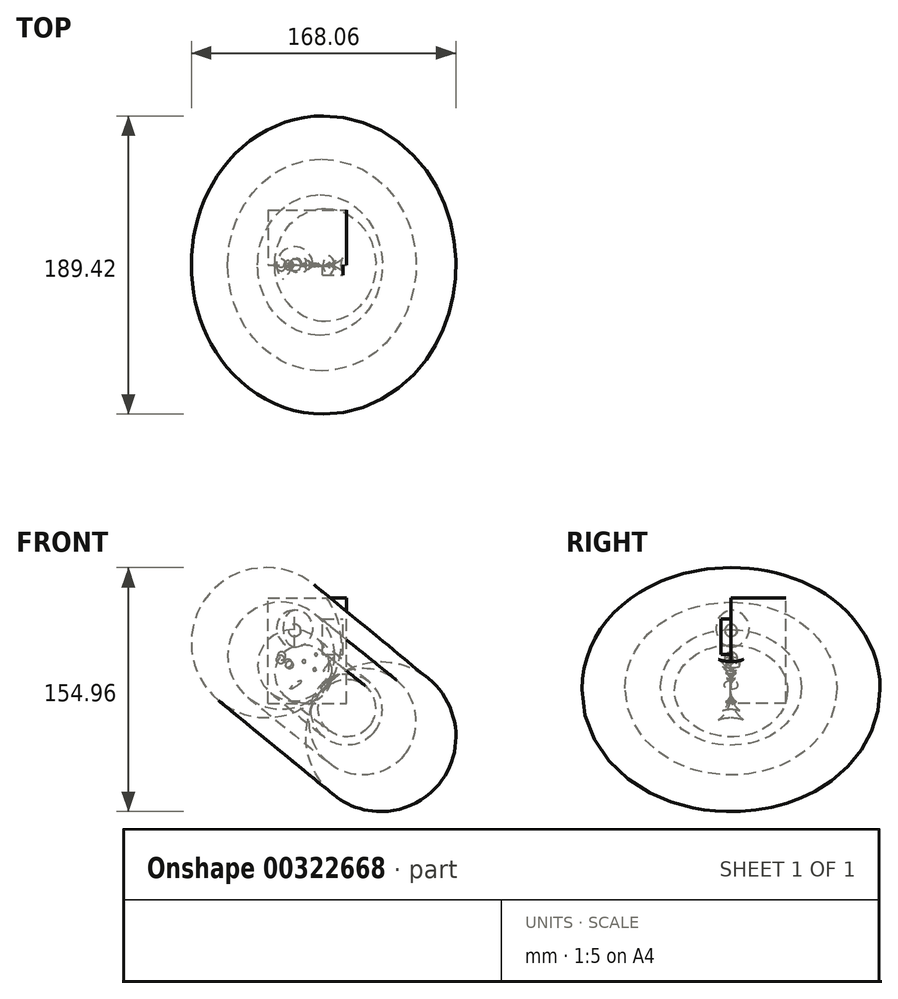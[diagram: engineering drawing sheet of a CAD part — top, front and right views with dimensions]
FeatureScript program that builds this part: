
annotation { "Feature Type Name" : "Feature", "Feature Type Description" : "" }
export const myFeature = defineFeature(function(context is Context, id is Id, definition is map)
    precondition{}
    {
        {
            var Q0;
            Q0=qCreatedBy(makeId("Front.planeOp"),FACE);
            var sketch = newSketch(context, id + "F0", { "sketchPlane" : qUnion([Q0])});
            skLineSegment(sketch, "E0.bottom", {"start": v(0, 0) * mm, "end": v(50, 0) * mm});
            skLineSegment(sketch, "E0.top", {"start": v(0, 67) * mm, "end": v(50, 67) * mm});
            skLineSegment(sketch, "E0.left", {"start": v(0, 0) * mm, "end": v(0, 67) * mm});
            skLineSegment(sketch, "E0.right", {"start": v(50, 0) * mm, "end": v(50, 67) * mm});
            skSolve(sketch);
        }
        {
            var Q0;
            Q0=makeQuery(id+"F0.imprint","IMPRINT",FACE,{"disambiguationData":[TD([[makeQuery(id+"F0.imprint","IMPRINT",EDGE,{"derivedFrom":sQuery(id+"F0.wireOp",EDGE,"E0.bottom")}),1.0]])]});
            extrude(context, id + "F1", {"entities" : qUnion([Q0]), "oppositeDirection" : true, "depth" : 35 * mm});
        }
        {
            var Q0;
            Q0=qCreatedBy(makeId("Front.planeOp"),FACE);
            var sketch = newSketch(context, id + "F2", { "sketchPlane" : qUnion([Q0])});
            skLineSegment(sketch, "E1", {"start": v(17.1, 35.74) * mm, "end": v(17.1, 59.12) * mm});
            skArc(sketch, "E2", {"start": v(17.1, 35.74) * mm, "mid": v(28.7, 47.43) * mm, "end": v(17.1, 59.12) * mm});
            skSolve(sketch);
        }
        {
            var Q0;
            Q0=makeQuery(id+"F2.imprint","IMPRINT",FACE,{"disambiguationData":[TD([[makeQuery(id+"F2.imprint","IMPRINT",EDGE,{"derivedFrom":sQuery(id+"F2.wireOp",EDGE,"E1")}),-1.0]])]});
            var Q1;
            Q1=sQuery(id+"F2.wireOp",EDGE,"E1");
            revolve(context, id + "F3", {"entities" : qUnion([Q0]), "axis" : qUnion([Q1]), "revolveType" : RevolveType.ONE_DIRECTION, "angle" : 232.55 * degree});
        }
        {
            var Q0;
            Q0=qCreatedBy(makeId("Front.planeOp"),FACE);
            var sketch = newSketch(context, id + "F4", { "sketchPlane" : qUnion([Q0])});
            skLineSegment(sketch, "E3", {"start": v(17.07, 42.3) * mm, "end": v(17.07, 50.09) * mm});
            skArc(sketch, "E4", {"start": v(17.07, 42.3) * mm, "mid": v(20.95, 46.19) * mm, "end": v(17.07, 50.09) * mm});
            skSolve(sketch);
        }
        {
            var Q0;
            Q0=makeQuery(id+"F4.imprint","IMPRINT",FACE,{"disambiguationData":[TD([[makeQuery(id+"F4.imprint","IMPRINT",EDGE,{"derivedFrom":sQuery(id+"F4.wireOp",EDGE,"E3")}),-1.0]])]});
            var Q1;
            Q1=sQuery(id+"F4.wireOp",EDGE,"E3");
            revolve(context, id + "F5", {"entities" : qUnion([Q0]), "axis" : qUnion([Q1]), "revolveType" : RevolveType.FULL});
        }
        {
            var Q0;
            Q0=makeQuery(id+"F1.opExtrude","CAP_FACE",FACE,{"disambiguationData":[OSD([sQuery(id+"F0.wireOp",EDGE,"E0.bottom"),sQuery(id+"F0.wireOp",EDGE,"E0.top"),sQuery(id+"F0.wireOp",EDGE,"E0.left"),sQuery(id+"F0.wireOp",EDGE,"E0.right")])],"isStart":true});
            var sketch = newSketch(context, id + "F6", { "sketchPlane" : qUnion([Q0])});
            skSolve(sketch);
        }
        {
            var Q0;
            Q0=makeQuery(id+"F6.imprint","IMPRINT",FACE,{"disambiguationData":[TD([[makeQuery(id+"F6.imprint","IMPRINT",EDGE,{"derivedFrom":makeQuery(id+"F1.opExtrude","CAP_EDGE",EDGE,{"disambiguationData":[OSD([sQuery(id+"F0.wireOp",EDGE,"E0.bottom")])],"isStart":true})}),1.0]])]});
            var sketch = newSketch(context, id + "F7", { "sketchPlane" : qUnion([Q0])});
            skLineSegment(sketch, "E5", {"start": v(10.7, 17.1) * mm, "end": v(10.7, 19.72) * mm});
            skFitSpline(sketch, "E6", {"points": [v(10.7, 17.1) * mm, v(18.18, 17.1) * mm, v(10.7, 19.72) * mm], "startDerivative": vector(22.57, -1.28) * mm, "endDerivative": vector(-22.36, 6.5) * mm});
            skSolve(sketch);
        }
        {
            var Q0;
            Q0=sQuery(id+"F7.wireOp",EDGE,"E6");
            var Q1;
            Q1=sQuery(id+"F7.wireOp",EDGE,"E5");
            revolve(context, id + "F8", {"bodyType" : ToolBodyType.SURFACE, "surfaceEntities" : qUnion([Q0]), "axis" : qUnion([Q1]), "revolveType" : RevolveType.FULL});
        }
        {
            var Q0;
            Q0=makeQuery(id+"F6.imprint","IMPRINT",FACE,{"disambiguationData":[TD([[makeQuery(id+"F6.imprint","IMPRINT",EDGE,{"derivedFrom":makeQuery(id+"F1.opExtrude","CAP_EDGE",EDGE,{"disambiguationData":[OSD([sQuery(id+"F0.wireOp",EDGE,"E0.bottom")])],"isStart":true})}),1.0]])]});
            var sketch = newSketch(context, id + "F9", { "sketchPlane" : qUnion([Q0])});
            skLineSegment(sketch, "E7", {"start": v(17.04, 12.85) * mm, "end": v(18.48, 10.81) * mm});
            skFitSpline(sketch, "E8", {"points": [v(18.48, 10.81) * mm, v(14.28, 9) * mm, v(17.04, 12.85) * mm], "startDerivative": vector(-11.93, -6.44) * mm, "endDerivative": vector(9, 10.46) * mm});
            skSolve(sketch);
        }
        {
            var Q0;
            Q0 = qSketchRegion(id + "F9", true);
            var Q1;
            Q1=sQuery(id+"F9.wireOp",EDGE,"E7");
            revolve(context, id + "F10", {"entities" : qUnion([Q0]), "axis" : qUnion([Q1]), "revolveType" : RevolveType.FULL});
        }
        {
            var Q0;
            Q0=makeQuery(id+"F6.imprint","IMPRINT",FACE,{"disambiguationData":[TD([[makeQuery(id+"F6.imprint","IMPRINT",EDGE,{"derivedFrom":makeQuery(id+"F1.opExtrude","CAP_EDGE",EDGE,{"disambiguationData":[OSD([sQuery(id+"F0.wireOp",EDGE,"E0.bottom")])],"isStart":true})}),1.0]])]});
            var sketch = newSketch(context, id + "F11", { "sketchPlane" : qUnion([Q0])});
            skLineSegment(sketch, "E9", {"start": v(29.76, 20.4) * mm, "end": v(29.76, 22.32) * mm});
            skArc(sketch, "E10", {"start": v(29.76, 20.4) * mm, "mid": v(30.8, 21.36) * mm, "end": v(29.76, 22.32) * mm});
            skSolve(sketch);
        }
        {
            var Q0;
            Q0=makeQuery(id+"F11.imprint","IMPRINT",FACE,{"disambiguationData":[TD([[makeQuery(id+"F11.imprint","IMPRINT",EDGE,{"derivedFrom":sQuery(id+"F11.wireOp",EDGE,"E9")}),-1.0]])]});
            var Q1;
            Q1=sQuery(id+"F11.wireOp",EDGE,"E9");
            revolve(context, id + "F12", {"entities" : qUnion([Q0]), "axis" : qUnion([Q1]), "revolveType" : RevolveType.FULL});
        }
        {
            var Q0;
            Q0=makeQuery(id+"F6.imprint","IMPRINT",FACE,{"disambiguationData":[TD([[makeQuery(id+"F6.imprint","IMPRINT",EDGE,{"derivedFrom":makeQuery(id+"F1.opExtrude","CAP_EDGE",EDGE,{"disambiguationData":[OSD([sQuery(id+"F0.wireOp",EDGE,"E0.bottom")])],"isStart":true})}),1.0]])]});
            var sketch = newSketch(context, id + "F13", { "sketchPlane" : qUnion([Q0])});
            skLineSegment(sketch, "E11", {"start": v(30.16, 30.2) * mm, "end": v(31.1, 31.55) * mm});
            skArc(sketch, "E12", {"start": v(30.16, 30.2) * mm, "mid": v(31.32, 30.4) * mm, "end": v(31.1, 31.55) * mm});
            skSolve(sketch);
        }
        {
            var Q0;
            Q0=makeQuery(id+"F13.imprint","IMPRINT",FACE,{"disambiguationData":[TD([[makeQuery(id+"F13.imprint","IMPRINT",EDGE,{"derivedFrom":sQuery(id+"F13.wireOp",EDGE,"E11")}),-1.0]])]});
            var Q1;
            Q1=sQuery(id+"F13.wireOp",EDGE,"E11");
            revolve(context, id + "F14", {"entities" : qUnion([Q0]), "axis" : qUnion([Q1]), "revolveType" : RevolveType.FULL});
        }
        {
            var Q0;
            Q0=makeQuery(id+"F6.imprint","IMPRINT",FACE,{"disambiguationData":[TD([[makeQuery(id+"F6.imprint","IMPRINT",EDGE,{"derivedFrom":makeQuery(id+"F1.opExtrude","CAP_EDGE",EDGE,{"disambiguationData":[OSD([sQuery(id+"F0.wireOp",EDGE,"E0.bottom")])],"isStart":true})}),1.0]])]});
            var sketch = newSketch(context, id + "F15", { "sketchPlane" : qUnion([Q0])});
            skLineSegment(sketch, "E13", {"start": v(22.2, 25.74) * mm, "end": v(23.76, 27.26) * mm});
            skArc(sketch, "E14", {"start": v(22.2, 25.74) * mm, "mid": v(23.73, 25.74) * mm, "end": v(23.76, 27.26) * mm});
            skSolve(sketch);
        }
        {
            var Q0;
            Q0=makeQuery(id+"F15.imprint","IMPRINT",FACE,{"disambiguationData":[TD([[makeQuery(id+"F15.imprint","IMPRINT",EDGE,{"derivedFrom":sQuery(id+"F15.wireOp",EDGE,"E13")}),-1.0]])]});
            var Q1;
            Q1=sQuery(id+"F15.wireOp",EDGE,"E13");
            revolve(context, id + "F16", {"entities" : qUnion([Q0]), "axis" : qUnion([Q1]), "revolveType" : RevolveType.FULL});
        }
        {
            var Q0;
            Q0=makeQuery(id+"F6.imprint","IMPRINT",FACE,{"disambiguationData":[TD([[makeQuery(id+"F6.imprint","IMPRINT",EDGE,{"derivedFrom":makeQuery(id+"F1.opExtrude","CAP_EDGE",EDGE,{"disambiguationData":[OSD([sQuery(id+"F0.wireOp",EDGE,"E0.bottom")])],"isStart":true})}),1.0]])]});
            var sketch = newSketch(context, id + "F17", { "sketchPlane" : qUnion([Q0])});
            skLineSegment(sketch, "E15", {"start": v(6.3, 29.55) * mm, "end": v(10.6, 28.29) * mm});
            skArc(sketch, "E16", {"start": v(10.6, 28.29) * mm, "mid": v(8.82, 30.2) * mm, "end": v(6.3, 29.55) * mm});
            skSolve(sketch);
        }
        {
            var Q0;
            Q0=makeQuery(id+"F17.imprint","IMPRINT",FACE,{"disambiguationData":[TD([[makeQuery(id+"F17.imprint","IMPRINT",EDGE,{"derivedFrom":sQuery(id+"F17.wireOp",EDGE,"E15")}),1.0]])]});
            var Q1;
            Q1=sQuery(id+"F17.wireOp",EDGE,"E15");
            revolve(context, id + "F18", {"entities" : qUnion([Q0]), "axis" : qUnion([Q1]), "revolveType" : RevolveType.FULL});
        }
        {
            var Q0;
            Q0=makeQuery(id+"F6.imprint","IMPRINT",FACE,{"disambiguationData":[TD([[makeQuery(id+"F6.imprint","IMPRINT",EDGE,{"derivedFrom":makeQuery(id+"F1.opExtrude","CAP_EDGE",EDGE,{"disambiguationData":[OSD([sQuery(id+"F0.wireOp",EDGE,"E0.bottom")])],"isStart":true})}),1.0]])]});
            var sketch = newSketch(context, id + "F19", { "sketchPlane" : qUnion([Q0])});
            skLineSegment(sketch, "E17", {"start": v(11.53, 23.44) * mm, "end": v(15.19, 26.28) * mm});
            skArc(sketch, "E18", {"start": v(11.53, 23.44) * mm, "mid": v(14.4, 23.53) * mm, "end": v(15.19, 26.28) * mm});
            skSolve(sketch);
        }
        {
            var Q0;
            Q0=makeQuery(id+"F19.imprint","IMPRINT",FACE,{"disambiguationData":[TD([[makeQuery(id+"F19.imprint","IMPRINT",EDGE,{"derivedFrom":sQuery(id+"F19.wireOp",EDGE,"E17")}),-1.0]])]});
            var Q1;
            Q1=sQuery(id+"F19.wireOp",EDGE,"E17");
            revolve(context, id + "F20", {"entities" : qUnion([Q0]), "axis" : qUnion([Q1]), "revolveType" : RevolveType.FULL});
        }
        {
            var Q0;
            Q0=makeQuery(id+"F6.imprint","IMPRINT",FACE,{"disambiguationData":[TD([[makeQuery(id+"F6.imprint","IMPRINT",EDGE,{"derivedFrom":makeQuery(id+"F1.opExtrude","CAP_EDGE",EDGE,{"disambiguationData":[OSD([sQuery(id+"F0.wireOp",EDGE,"E0.bottom")])],"isStart":true})}),1.0]])]});
            var sketch = newSketch(context, id + "F21", { "sketchPlane" : qUnion([Q0])});
            skLineSegment(sketch, "E19", {"start": v(29.62, 5.76) * mm, "end": v(36.7, 14.27) * mm});
            skArc(sketch, "E20", {"start": v(29.62, 5.76) * mm, "mid": v(33.68, 9.58) * mm, "end": v(36.7, 14.27) * mm});
            skSolve(sketch);
        }
        {
            var Q0;
            Q0=makeQuery(id+"F21.imprint","IMPRINT",FACE,{"disambiguationData":[TD([[makeQuery(id+"F21.imprint","IMPRINT",EDGE,{"derivedFrom":sQuery(id+"F21.wireOp",EDGE,"E19")}),-1.0]])]});
            var Q1;
            Q1=sQuery(id+"F21.wireOp",EDGE,"E19");
            revolve(context, id + "F22", {"entities" : qUnion([Q0]), "axis" : qUnion([Q1]), "revolveType" : RevolveType.FULL});
        }
        {
            var Q0;
            Q0=makeQuery(id+"F6.imprint","IMPRINT",FACE,{"disambiguationData":[TD([[makeQuery(id+"F6.imprint","IMPRINT",EDGE,{"derivedFrom":makeQuery(id+"F1.opExtrude","CAP_EDGE",EDGE,{"disambiguationData":[OSD([sQuery(id+"F0.wireOp",EDGE,"E0.bottom")])],"isStart":true})}),1.0]])]});
            var sketch = newSketch(context, id + "F23", { "sketchPlane" : qUnion([Q0])});
            skLineSegment(sketch, "E21", {"start": v(30.12, 3.98) * mm, "end": v(38.66, 14.55) * mm});
            skArc(sketch, "E22", {"start": v(38.66, 14.55) * mm, "mid": v(33.85, 9.7) * mm, "end": v(30.12, 3.98) * mm});
            skSolve(sketch);
        }
        {
            var Q0;
            Q0=makeQuery(id+"F23.imprint","IMPRINT",FACE,{"disambiguationData":[TD([[makeQuery(id+"F23.imprint","IMPRINT",EDGE,{"derivedFrom":sQuery(id+"F23.wireOp",EDGE,"E21")}),1.0]])]});
            var Q1;
            Q1=sQuery(id+"F23.wireOp",EDGE,"E21");
            revolve(context, id + "F24", {"entities" : qUnion([Q0]), "axis" : qUnion([Q1]), "revolveType" : RevolveType.FULL});
        }
        {
            var Q0;
            Q0=makeQuery(id+"F6.imprint","IMPRINT",FACE,{"disambiguationData":[TD([[makeQuery(id+"F6.imprint","IMPRINT",EDGE,{"derivedFrom":makeQuery(id+"F1.opExtrude","CAP_EDGE",EDGE,{"disambiguationData":[OSD([sQuery(id+"F0.wireOp",EDGE,"E0.bottom")])],"isStart":true})}),1.0]])]});
            var sketch = newSketch(context, id + "F25", { "sketchPlane" : qUnion([Q0])});
            skLineSegment(sketch, "E23", {"start": v(30.91, 3.08) * mm, "end": v(40, 14.16) * mm});
            skArc(sketch, "E24", {"start": v(40, 14.16) * mm, "mid": v(35.04, 8.96) * mm, "end": v(30.91, 3.08) * mm});
            skSolve(sketch);
        }
        {
            var Q0;
            Q0=makeQuery(id+"F25.imprint","IMPRINT",FACE,{"disambiguationData":[TD([[makeQuery(id+"F25.imprint","IMPRINT",EDGE,{"derivedFrom":sQuery(id+"F25.wireOp",EDGE,"E23")}),1.0]])]});
            var Q1;
            Q1=sQuery(id+"F25.wireOp",EDGE,"E23");
            revolve(context, id + "F26", {"entities" : qUnion([Q0]), "axis" : qUnion([Q1]), "revolveType" : RevolveType.FULL});
        }
        {
            var Q0;
            Q0=makeQuery(id+"F6.imprint","IMPRINT",FACE,{"disambiguationData":[TD([[makeQuery(id+"F6.imprint","IMPRINT",EDGE,{"derivedFrom":makeQuery(id+"F1.opExtrude","CAP_EDGE",EDGE,{"disambiguationData":[OSD([sQuery(id+"F0.wireOp",EDGE,"E0.bottom")])],"isStart":true})}),1.0]])]});
            var sketch = newSketch(context, id + "F27", { "sketchPlane" : qUnion([Q0])});
            skLineSegment(sketch, "E25", {"start": v(33.24, 3.6) * mm, "end": v(39.79, 11.94) * mm});
            skArc(sketch, "E26", {"start": v(39.79, 11.94) * mm, "mid": v(35.9, 8.25) * mm, "end": v(33.24, 3.6) * mm});
            skSolve(sketch);
        }
        {
            var Q0;
            Q0=makeQuery(id+"F27.imprint","IMPRINT",FACE,{"disambiguationData":[TD([[makeQuery(id+"F27.imprint","IMPRINT",EDGE,{"derivedFrom":sQuery(id+"F27.wireOp",EDGE,"E25")}),1.0]])]});
            var Q1;
            Q1=sQuery(id+"F27.wireOp",EDGE,"E25");
            revolve(context, id + "F28", {"entities" : qUnion([Q0]), "axis" : qUnion([Q1]), "revolveType" : RevolveType.FULL});
        }
        {
            var Q0;
            Q0=makeQuery(id+"F6.imprint","IMPRINT",FACE,{"disambiguationData":[TD([[makeQuery(id+"F6.imprint","IMPRINT",EDGE,{"derivedFrom":makeQuery(id+"F1.opExtrude","CAP_EDGE",EDGE,{"disambiguationData":[OSD([sQuery(id+"F0.wireOp",EDGE,"E0.bottom")])],"isStart":true})}),1.0]])]});
            var sketch = newSketch(context, id + "F29", { "sketchPlane" : qUnion([Q0])});
            skLineSegment(sketch, "E27.bottom", {"start": v(34.67, 31) * mm, "end": v(47.68, 31) * mm});
            skLineSegment(sketch, "E27.top", {"start": v(34.67, 53.64) * mm, "end": v(47.68, 53.64) * mm});
            skLineSegment(sketch, "E27.left", {"start": v(34.67, 31) * mm, "end": v(34.67, 53.64) * mm});
            skLineSegment(sketch, "E27.right", {"start": v(47.68, 31) * mm, "end": v(47.68, 53.64) * mm});
            skSolve(sketch);
        }
        {
            var Q0;
            Q0=makeQuery(id+"F29.imprint","IMPRINT",FACE,{"disambiguationData":[TD([[makeQuery(id+"F29.imprint","IMPRINT",EDGE,{"derivedFrom":sQuery(id+"F29.wireOp",EDGE,"E27.bottom")}),1.0]])]});
            extrude(context, id + "F30", {"entities" : qUnion([Q0]), "depth" : 6.35 * mm});
        }
        {
            var Q0;
            Q0=makeQuery(id+"F6.imprint","IMPRINT",FACE,{"disambiguationData":[TD([[makeQuery(id+"F6.imprint","IMPRINT",EDGE,{"derivedFrom":makeQuery(id+"F1.opExtrude","CAP_EDGE",EDGE,{"disambiguationData":[OSD([sQuery(id+"F0.wireOp",EDGE,"E0.bottom")])],"isStart":true})}),1.0]])]});
            var sketch = newSketch(context, id + "F31", { "sketchPlane" : qUnion([Q0])});
            skLineSegment(sketch, "E28", {"start": v(38.29, 25.2) * mm, "end": v(39.41, 24.32) * mm});
            skFitSpline(sketch, "E29", {"points": [v(38.29, 25.2) * mm, v(42.22, 29.44) * mm, v(39.41, 24.32) * mm], "startDerivative": vector(11.24, 13.2) * mm, "endDerivative": vector(-8.98, -14.92) * mm});
            skSolve(sketch);
        }
        {
            var Q0;
            Q0=makeQuery(id+"F31.imprint","IMPRINT",FACE,{"disambiguationData":[TD([[makeQuery(id+"F31.imprint","IMPRINT",EDGE,{"derivedFrom":sQuery(id+"F31.wireOp",EDGE,"E28")}),1.0]])]});
            var Q1;
            Q1=sQuery(id+"F31.wireOp",EDGE,"E28");
            revolve(context, id + "F32", {"entities" : qUnion([Q0]), "axis" : qUnion([Q1]), "revolveType" : RevolveType.FULL});
        }
    });
